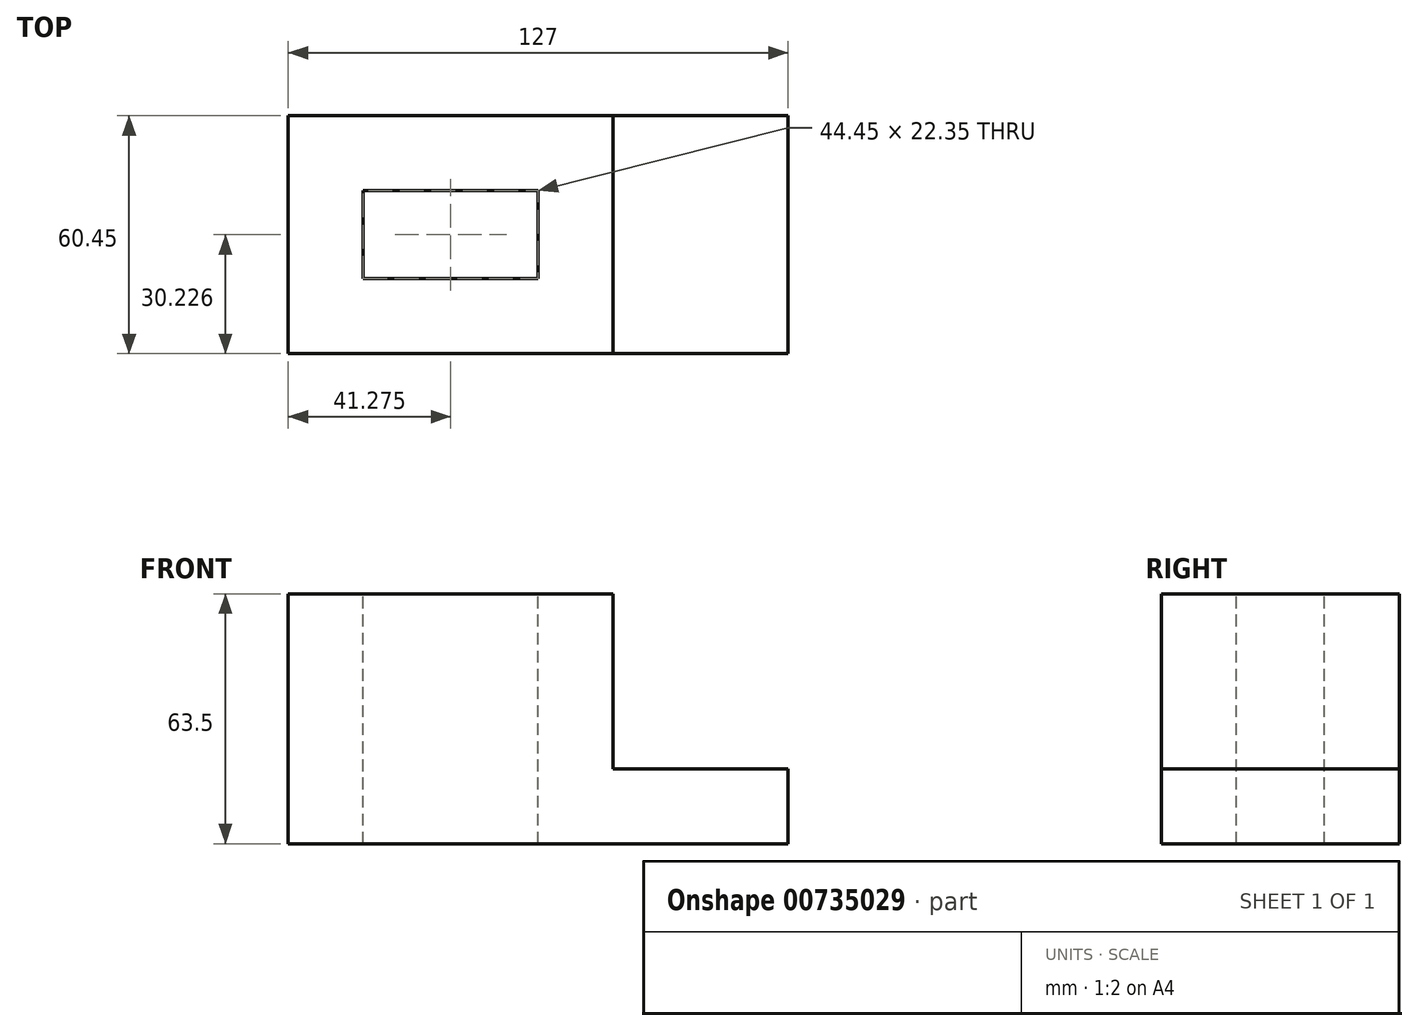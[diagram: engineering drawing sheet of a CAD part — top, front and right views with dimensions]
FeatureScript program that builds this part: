
annotation { "Feature Type Name" : "Feature", "Feature Type Description" : "" }
export const myFeature = defineFeature(function(context is Context, id is Id, definition is map)
    precondition{}
    {
        {
            var Q0;
            Q0=qCreatedBy(makeId("Top.planeOp"),FACE);
            var sketch = newSketch(context, id + "F0", { "sketchPlane" : qUnion([Q0])});
            skLineSegment(sketch, "E0.bottom", {"start": v(0, 0) * mm, "end": v(127, 0) * mm});
            skLineSegment(sketch, "E0.top", {"start": v(0, 60.45) * mm, "end": v(127, 60.45) * mm});
            skLineSegment(sketch, "E0.left", {"start": v(0, 0) * mm, "end": v(0, 60.45) * mm});
            skLineSegment(sketch, "E0.right", {"start": v(127, 0) * mm, "end": v(127, 60.45) * mm});
            skSolve(sketch);
        }
        {
            var Q0;
            Q0=makeQuery(id+"F0.imprint","IMPRINT",FACE,{"disambiguationData":[TD([[makeQuery(id+"F0.imprint","IMPRINT",EDGE,{"derivedFrom":sQuery(id+"F0.wireOp",EDGE,"E0.bottom")}),1.0]])]});
            extrude(context, id + "F1", {"entities" : qUnion([Q0]), "depth" : 63.5 * mm, "offsetDistance" : 25.4 * mm});
        }
        {
            var Q0;
            Q0=makeQuery(id+"F1.opExtrude","CAP_FACE",FACE,{"disambiguationData":[OSD([sQuery(id+"F0.wireOp",EDGE,"E0.bottom"),sQuery(id+"F0.wireOp",EDGE,"E0.top"),sQuery(id+"F0.wireOp",EDGE,"E0.left"),sQuery(id+"F0.wireOp",EDGE,"E0.right")])],"isStart":false});
            var sketch = newSketch(context, id + "F2", { "sketchPlane" : qUnion([Q0])});
            skLineSegment(sketch, "E1.bottom", {"start": v(19.05, 41.4) * mm, "end": v(63.5, 41.4) * mm});
            skLineSegment(sketch, "E1.top", {"start": v(19.05, 19.05) * mm, "end": v(63.5, 19.05) * mm});
            skLineSegment(sketch, "E1.left", {"start": v(19.05, 41.4) * mm, "end": v(19.05, 19.05) * mm});
            skLineSegment(sketch, "E1.right", {"start": v(63.5, 41.4) * mm, "end": v(63.5, 19.05) * mm});
            skSolve(sketch);
        }
        {
            var Q0;
            Q0=makeQuery(id+"F2.imprint","IMPRINT",FACE,{"disambiguationData":[TD([[makeQuery(id+"F2.imprint","IMPRINT",EDGE,{"derivedFrom":sQuery(id+"F2.wireOp",EDGE,"E1.bottom")}),-1.0]])]});
            extrude(context, id + "F3", {"entities" : qUnion([Q0]), "operationType" : NewBodyOperationType.REMOVE, "endBound" : BoundingType.THROUGH_ALL, "oppositeDirection" : true, "depth" : 63.5 * mm, "offsetDistance" : 25.4 * mm});
        }
        {
            var Q0;
            Q0=makeQuery(id+"F1.opExtrude","SWEPT_FACE",FACE,{"disambiguationData":[OSD([sQuery(id+"F0.wireOp",EDGE,"E0.bottom")])]});
            var sketch = newSketch(context, id + "F4", { "sketchPlane" : qUnion([Q0])});
            skLineSegment(sketch, "E2.bottom", {"start": v(127, 63.5) * mm, "end": v(82.55, 63.5) * mm});
            skLineSegment(sketch, "E2.top", {"start": v(127, 19.05) * mm, "end": v(82.55, 19.05) * mm});
            skLineSegment(sketch, "E2.left", {"start": v(127, 63.5) * mm, "end": v(127, 19.05) * mm});
            skLineSegment(sketch, "E2.right", {"start": v(82.55, 63.5) * mm, "end": v(82.55, 19.05) * mm});
            skSolve(sketch);
        }
        {
            var Q0;
            Q0 = qSketchRegion(id + "F4", true);
            extrude(context, id + "F5", {"entities" : qUnion([Q0]), "operationType" : NewBodyOperationType.REMOVE, "oppositeDirection" : true, "depth" : 63.5 * mm, "offsetDistance" : 25.4 * mm});
        }
    });
